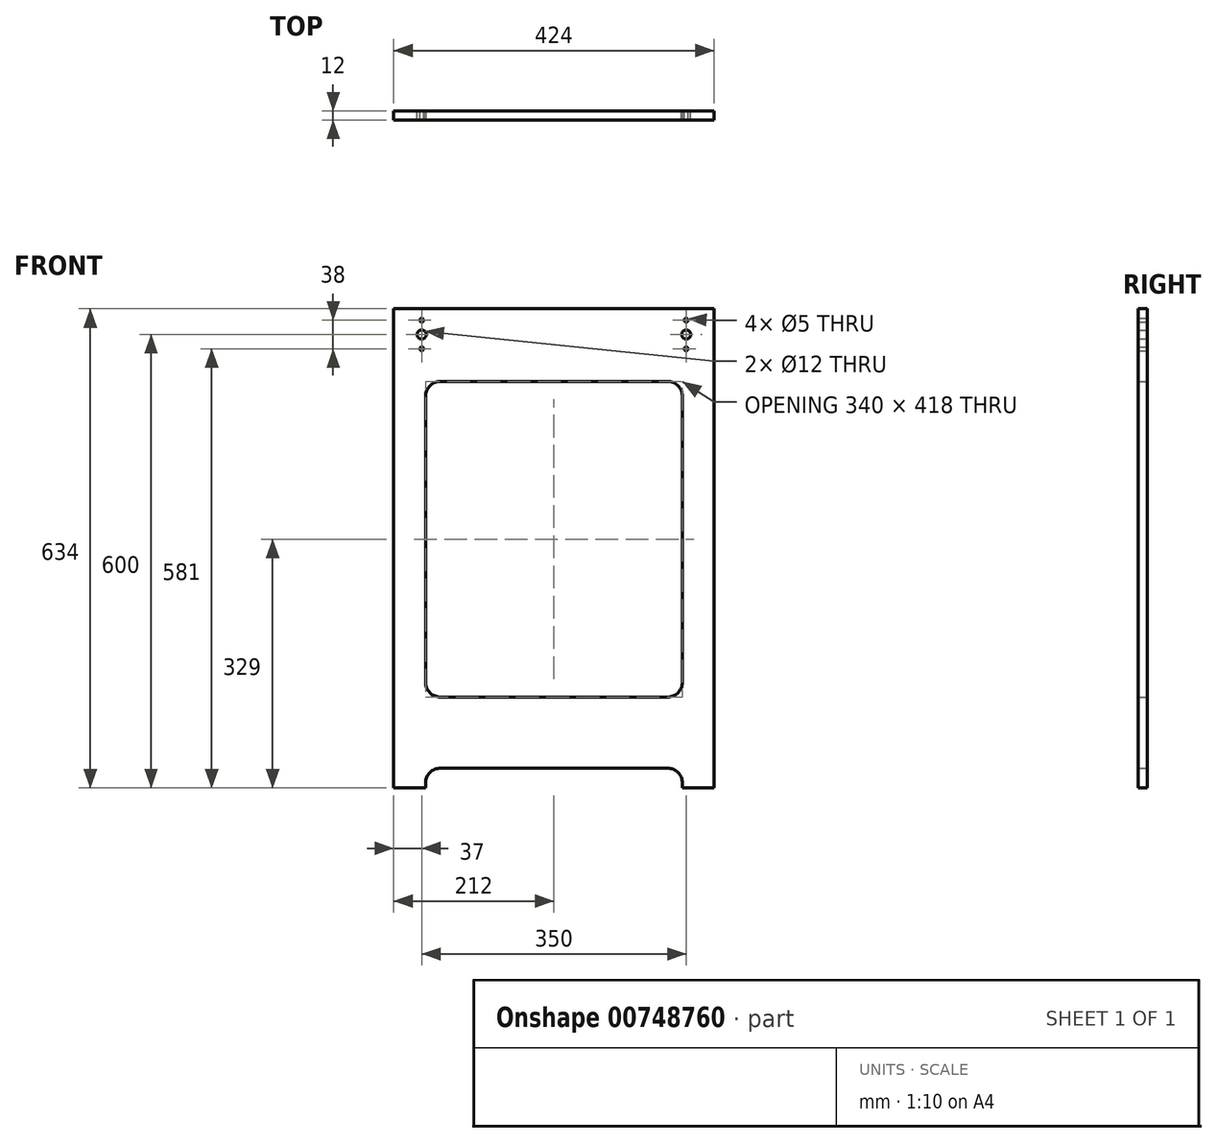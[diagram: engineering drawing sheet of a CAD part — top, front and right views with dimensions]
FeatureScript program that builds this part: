
annotation { "Feature Type Name" : "Feature", "Feature Type Description" : "" }
export const myFeature = defineFeature(function(context is Context, id is Id, definition is map)
    precondition{}
    {
        {
            assignVariable(context, id + "F0", {"name" : "Width", "anyValue" : 12});
        }
        {
            var Q0;
            Q0=qCreatedBy(makeId("Front.planeOp"),FACE);
            var sketch = newSketch(context, id + "F1", { "sketchPlane" : qUnion([Q0])});
            skLineSegment(sketch, "E0.bottom", {"start": v(200, 374) * mm, "end": v(-200, 374) * mm});
            skLineSegment(sketch, "E0.top", {"start": v(200, -260) * mm, "end": v(-200, -260) * mm});
            skLineSegment(sketch, "E0.left", {"start": v(200, 374) * mm, "end": v(200, -260) * mm});
            skLineSegment(sketch, "E0.right", {"start": v(-200, 374) * mm, "end": v(-200, -260) * mm});
            skLineSegment(sketch, "E1.bottom", {"start": v(150, 278) * mm, "end": v(-150, 278) * mm});
            skLineSegment(sketch, "E1.top", {"start": v(150, -140) * mm, "end": v(-150, -140) * mm});
            skLineSegment(sketch, "E1.left", {"start": v(170, 258) * mm, "end": v(170, -120) * mm});
            skLineSegment(sketch, "E1.right", {"start": v(-170, 258) * mm, "end": v(-170, -120) * mm});
            skPoint(sketch, "E1.middle", {"position": v(0, 0) * mm});
            skCircle(sketch, "E2", {"center": v(175, 340) * mm, "radius": 6 * mm});
            skCircle(sketch, "E3", {"center": v(-175, 340) * mm, "radius": 6 * mm});
            skLineSegment(sketch, "E4", {"start": v(200, -150) * mm, "end": v(-200, -150) * mm});
            skLineSegment(sketch, "E5", {"start": v(-200, -150) * mm, "end": v(-200, -162) * mm});
            skLineSegment(sketch, "E6", {"start": v(-200, -162) * mm, "end": v(200, -162) * mm});
            skLineSegment(sketch, "E7", {"start": v(200, -162) * mm, "end": v(200, -150) * mm});
            skLineSegment(sketch, "E8", {"start": v(-200, -260) * mm, "end": v(-212, -260) * mm});
            skLineSegment(sketch, "E9", {"start": v(-212, -260) * mm, "end": v(-212, 374) * mm});
            skLineSegment(sketch, "E10", {"start": v(-212, 374) * mm, "end": v(-200, 374) * mm});
            skLineSegment(sketch, "E11", {"start": v(200, 374) * mm, "end": v(212, 374) * mm});
            skLineSegment(sketch, "E12", {"start": v(212, 374) * mm, "end": v(212, -260) * mm});
            skLineSegment(sketch, "E13", {"start": v(212, -260) * mm, "end": v(200, -260) * mm});
            skLineSegment(sketch, "E14", {"start": v(-200, -222) * mm, "end": v(200, -222) * mm});
            skLineSegment(sketch, "E15", {"start": v(200, -222) * mm, "end": v(200, -234) * mm});
            skLineSegment(sketch, "E16", {"start": v(-200, -234) * mm, "end": v(-200, -222) * mm});
            skPoint(sketch, "E17.visualSharp", {"position": v(170, 278) * mm});
            skArc(sketch, "E17.filletArc", {"start": v(170, 258) * mm, "mid": v(164.14, 272.14) * mm, "end": v(150, 278) * mm});
            skPoint(sketch, "E18.visualSharp", {"position": v(-170, 278) * mm});
            skArc(sketch, "E18.filletArc", {"start": v(-150, 278) * mm, "mid": v(-164.14, 272.14) * mm, "end": v(-170, 258) * mm});
            skPoint(sketch, "E19.visualSharp", {"position": v(170, -140) * mm});
            skArc(sketch, "E19.filletArc", {"start": v(150, -140) * mm, "mid": v(164.14, -134.14) * mm, "end": v(170, -120) * mm});
            skPoint(sketch, "E20.visualSharp", {"position": v(-170, -140) * mm});
            skArc(sketch, "E20.filletArc", {"start": v(-170, -120) * mm, "mid": v(-164.14, -134.14) * mm, "end": v(-150, -140) * mm});
            skLineSegment(sketch, "E21", {"start": v(-170, -254) * mm, "end": v(-170, -260) * mm});
            skLineSegment(sketch, "E22", {"start": v(170, -254) * mm, "end": v(170, -260) * mm});
            skLineSegment(sketch, "E23", {"start": v(-150, -234) * mm, "end": v(150, -234) * mm});
            skArc(sketch, "E24.filletArc", {"start": v(170, -254) * mm, "mid": v(164.14, -239.86) * mm, "end": v(150, -234) * mm});
            skArc(sketch, "E25.filletArc", {"start": v(-150, -234) * mm, "mid": v(-164.14, -239.86) * mm, "end": v(-170, -254) * mm});
            skLineSegment(sketch, "E26", {"start": v(-200, -234) * mm, "end": v(-150, -234) * mm});
            skLineSegment(sketch, "E27", {"start": v(150, -234) * mm, "end": v(200, -234) * mm});
            skCircle(sketch, "E28", {"center": v(-175, 359) * mm, "radius": 2.5 * mm});
            skCircle(sketch, "E29", {"center": v(-175, 321) * mm, "radius": 2.5 * mm});
            skCircle(sketch, "E30", {"center": v(175, 359) * mm, "radius": 2.5 * mm});
            skCircle(sketch, "E31", {"center": v(175, 321) * mm, "radius": 2.5 * mm});
            skSolve(sketch);
        }
        {
            var Q0;
            {var subQ0=sQuery(id+"F1.wireOp",EDGE,"E0.bottom");Q0=makeQuery(id+"F1.imprint","IMPRINT",FACE,{"disambiguationData":[TD([[makeQuery(id+"F1.imprint","IMPRINT",EDGE,{"derivedFrom":subQ0}),1.0]])]});}
            var Q1;
            {var subQ5=sQuery(id+"F1.wireOp",EDGE,"E11");Q1=makeQuery(id+"F1.imprint","IMPRINT",FACE,{"disambiguationData":[TD([[makeQuery(id+"F1.imprint","IMPRINT",EDGE,{"derivedFrom":subQ5}),-1.0]])]});}
            var Q2;
            {var subQ4=sQuery(id+"F1.wireOp",EDGE,"E8");Q2=makeQuery(id+"F1.imprint","IMPRINT",FACE,{"disambiguationData":[TD([[makeQuery(id+"F1.imprint","IMPRINT",EDGE,{"derivedFrom":subQ4}),-1.0]])]});}
            var Q3;
            {var subQ2=sQuery(id+"F1.wireOp",EDGE,"E4");Q3=makeQuery(id+"F1.imprint","IMPRINT",FACE,{"disambiguationData":[TD([[makeQuery(id+"F1.imprint","IMPRINT",EDGE,{"derivedFrom":subQ2}),1.0]])]});}
            var Q4;
            {var subQ0=sQuery(id+"F1.wireOp",EDGE,"E6");Q4=makeQuery(id+"F1.imprint","IMPRINT",FACE,{"disambiguationData":[TD([[makeQuery(id+"F1.imprint","IMPRINT",EDGE,{"derivedFrom":subQ0}),-1.0]])]});}
            var Q5;
            {var subQ2=sQuery(id+"F1.wireOp",EDGE,"E14");Q5=makeQuery(id+"F1.imprint","IMPRINT",FACE,{"disambiguationData":[TD([[makeQuery(id+"F1.imprint","IMPRINT",EDGE,{"derivedFrom":subQ2}),-1.0]])]});}
            var Q6;
            {var subQ0=sQuery(id+"F1.wireOp",EDGE,"E21");Q6=makeQuery(id+"F1.imprint","IMPRINT",FACE,{"disambiguationData":[TD([[makeQuery(id+"F1.imprint","IMPRINT",EDGE,{"derivedFrom":subQ0}),-1.0]])]});}
            var Q7;
            {var subQ0=sQuery(id+"F1.wireOp",EDGE,"E22");Q7=makeQuery(id+"F1.imprint","IMPRINT",FACE,{"disambiguationData":[TD([[makeQuery(id+"F1.imprint","IMPRINT",EDGE,{"derivedFrom":subQ0}),1.0]])]});}
            extrude(context, id + "F2", {"entities" : qUnion([Q0, Q1, Q2, Q3, Q4, Q5, Q6, Q7]), "depth" : (getVariable(context, 'Width')) * mm, "offsetDistance" : 25 * mm});
        }
    });
